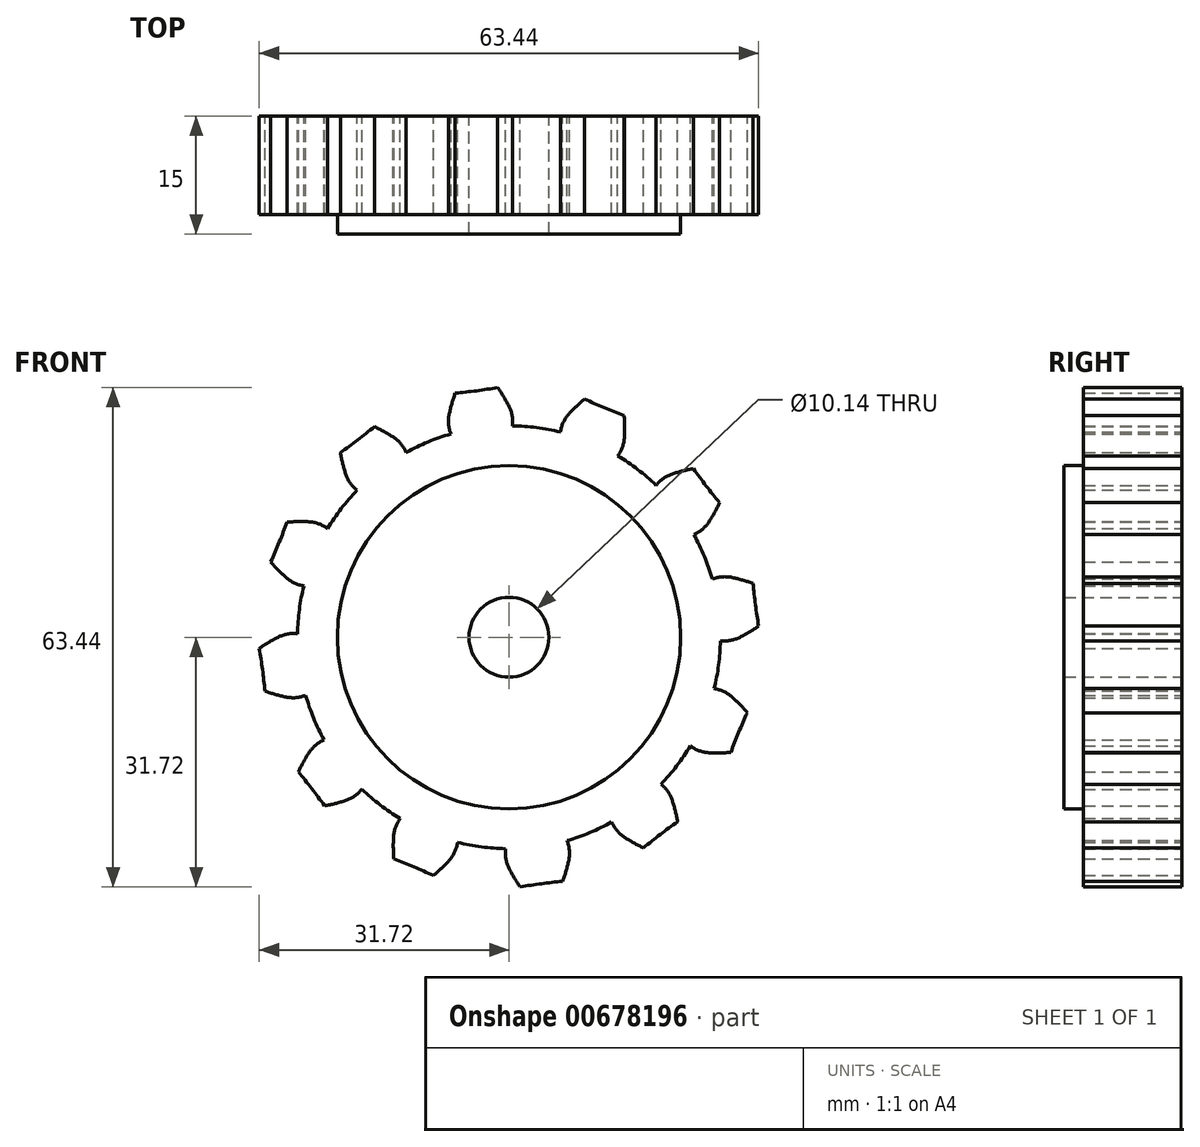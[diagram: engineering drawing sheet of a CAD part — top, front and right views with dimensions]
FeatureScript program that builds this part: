
annotation { "Feature Type Name" : "Feature", "Feature Type Description" : "" }
export const myFeature = defineFeature(function(context is Context, id is Id, definition is map)
    precondition{}
    {
        {
            var Q0;
            Q0=qCreatedBy(makeId("Front.planeOp"),FACE);
            var sketch = newSketch(context, id + "F0", { "sketchPlane" : qUnion([Q0])});
            skCircle(sketch, "E0", {"center": v(0, 0) * mm, "radius": 26.86 * mm});
            skCircle(sketch, "E1", {"center": v(0, 0) * mm, "radius": 29.34 * mm, "construction": true});
            skCircle(sketch, "E2", {"center": v(0, 0) * mm, "radius": 31.75 * mm, "construction": true});
            skLineSegment(sketch, "E3", {"start": v(0, 0) * mm, "end": v(0, 72.49) * mm, "construction": true});
            skLineSegment(sketch, "E4", {"start": v(0, 0) * mm, "end": v(-10.47, 79.5) * mm, "construction": true});
            skLineSegment(sketch, "E5", {"start": v(0, 29.34) * mm, "end": v(-56.45, 29.34) * mm, "construction": true});
            skLineSegment(sketch, "E6", {"start": v(0, 29.34) * mm, "end": v(-56.45, 8.8) * mm, "construction": true});
            skCircle(sketch, "E7", {"center": v(0, 0) * mm, "radius": 27.57 * mm, "construction": true});
            skCircle(sketch, "E8", {"center": v(0, 29.34) * mm, "radius": 7.3 * mm, "construction": true});
            skCircle(sketch, "E9", {"center": v(-6.86, 26.84) * mm, "radius": 7.3 * mm, "construction": true});
            skArc(sketch, "E10", {"start": v(0, 29.34) * mm, "mid": v(-0.67, 30.55) * mm, "end": v(-1.43, 31.72) * mm});
            skArc(sketch, "E11", {"start": v(0.44, 26.86) * mm, "mid": v(0.4, 28.13) * mm, "end": v(0, 29.34) * mm});
            skArc(sketch, "E12.MirrorCS", {"start": v(-7.6, 28.34) * mm, "mid": v(-7.26, 29.69) * mm, "end": v(-6.83, 31) * mm});
            skArc(sketch, "E13.MirrorCS", {"start": v(-7.38, 25.83) * mm, "mid": v(-7.67, 27.07) * mm, "end": v(-7.6, 28.34) * mm});
            skArc(sketch, "E14", {"start": v(-6.83, 31) * mm, "mid": v(-4.12, 31.3) * mm, "end": v(-1.43, 31.72) * mm});
            skCircle(sketch, "E15", {"center": v(0, 0) * mm, "radius": 21.8 * mm});
            skLineSegment(sketch, "E16", {"start": v(0, 0) * mm, "end": v(4.78, 6.29) * mm});
            skLineSegment(sketch, "E17", {"start": v(0, -5.17) * mm, "end": v(-7.89, 3.58) * mm});
            skCircle(sketch, "E18", {"center": v(0, 0) * mm, "radius": 5.07 * mm});
            skSolve(sketch);
        }
        {
            var Q0;
            {var subQ0=sQuery(id+"F0.wireOp",EDGE,"E0");var subQ1=makeQuery(id+"F0.imprint","INTERSECT",VERTEX,{"derivedFrom":[subQ0,sQuery(id+"F0.wireOp",EDGE,"E11")]});Q0=makeQuery(id+"F0.imprint","IMPRINT",FACE,{"disambiguationData":[TD([[makeQuery(id+"F0.imprint","IMPRINT",EDGE,{"disambiguationData":[TD([[subQ1,-1.0]])],"derivedFrom":subQ0}),1.0]])]});}
            var Q1;
            Q1=makeQuery(id+"F0.imprint","IMPRINT",FACE,{"disambiguationData":[TD([[makeQuery(id+"F0.imprint","IMPRINT",EDGE,{"derivedFrom":sQuery(id+"F0.wireOp",EDGE,"E10")}),1.0]])]});
            extrude(context, id + "F1", {"entities" : qUnion([Q0, Q1]), "depth" : 12.5 * mm, "offsetDistance" : 25 * mm});
        }
        {
            var Q0;
            Q0=makeQuery(id+"F1.opExtrude","SWEPT_BODY",BODY,{"disambiguationData":[OSD([sQuery(id+"F0.wireOp",EDGE,"E0"),sQuery(id+"F0.wireOp",EDGE,"E10"),sQuery(id+"F0.wireOp",EDGE,"E11"),sQuery(id+"F0.wireOp",EDGE,"E12.MirrorCS"),sQuery(id+"F0.wireOp",EDGE,"E13.MirrorCS"),sQuery(id+"F0.wireOp",EDGE,"E14")])]});
            var Q1;
            Q1=makeQuery(id+"F1.opExtrude","SWEPT_FACE",FACE,{"disambiguationData":[OSD([sQuery(id+"F0.wireOp",EDGE,"E0")])]});
            circularPattern(context, id + "F2", {"entities" : qUnion([Q0]), "axis" : qUnion([Q1]), "angle" : 360 * degree, "instanceCount" : 12, "equalSpace" : true});
        }
        {
            var Q0;
            Q0=makeQuery(id+"F0.imprint","IMPRINT",FACE,{"disambiguationData":[TD([[makeQuery(id+"F0.imprint","IMPRINT",EDGE,{"derivedFrom":sQuery(id+"F0.wireOp",EDGE,"E15")}),1.0]])]});
            extrude(context, id + "F3", {"entities" : qUnion([Q0]), "operationType" : NewBodyOperationType.ADD, "depth" : 15 * mm, "offsetDistance" : 25 * mm});
        }
    });
